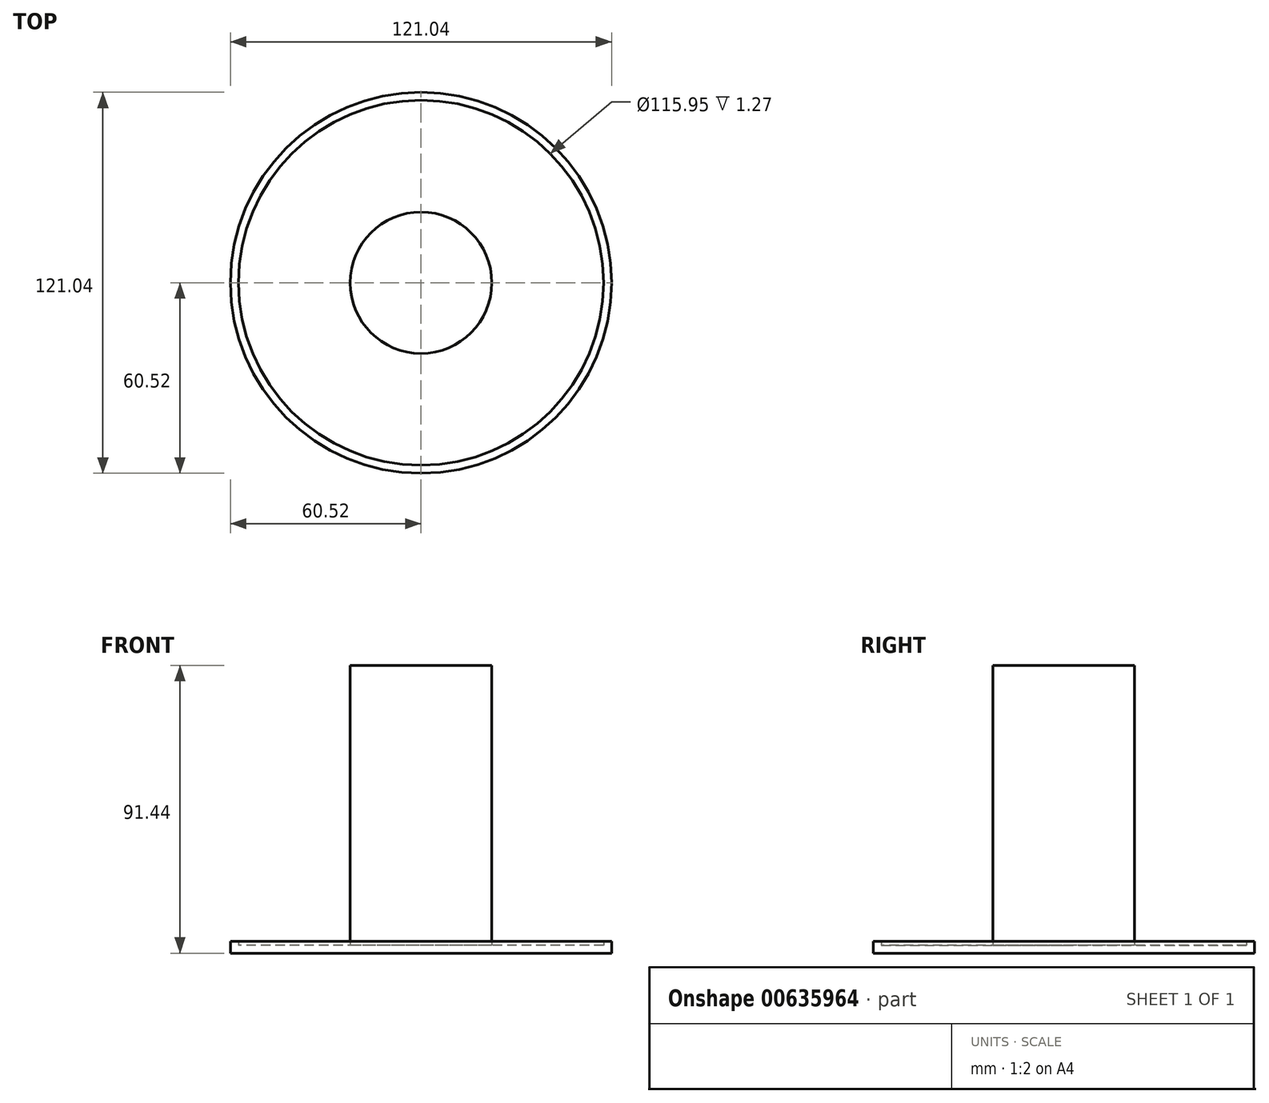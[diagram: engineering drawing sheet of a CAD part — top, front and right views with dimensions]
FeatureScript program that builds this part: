
annotation { "Feature Type Name" : "Feature", "Feature Type Description" : "" }
export const myFeature = defineFeature(function(context is Context, id is Id, definition is map)
    precondition{}
    {
        {
            var Q0;
            Q0=qCreatedBy(makeId("Top.planeOp"),FACE);
            var sketch = newSketch(context, id + "F0", { "sketchPlane" : qUnion([Q0])});
            skCircle(sketch, "E0", {"center": v(0, 0) * mm, "radius": 60.52 * mm});
            skSolve(sketch);
        }
        {
            var Q0;
            Q0 = qSketchRegion(id + "F0", true);
            extrude(context, id + "F1", {"entities" : qUnion([Q0]), "depth" : 3.8 * mm, "offsetDistance" : 25.4 * mm});
        }
        {
            var Q0;
            Q0=makeQuery(id+"F1.opExtrude","CAP_FACE",FACE,{"disambiguationData":[OSD([sQuery(id+"F0.wireOp",EDGE,"E0")])],"isStart":false});
            shell(context, id + "F2", {"entities" : qUnion([Q0]), "thickness" : 2.54 * mm});
        }
        {
            var Q0;
            {var subQ0=sQuery(id+"F0.wireOp",EDGE,"E0");Q0=makeQuery(id+"F2.opShell","OFFSET_FACE",FACE,{"disambiguationData":[OSD([subQ0]),TDD([makeQuery(id+"F1.opExtrude","CAP_FACE",FACE,{"disambiguationData":[OSD([subQ0])],"isStart":true})])]});}
            var sketch = newSketch(context, id + "F3", { "sketchPlane" : qUnion([Q0])});
            skCircle(sketch, "E1", {"center": v(0, 0) * mm, "radius": 22.48 * mm});
            skSolve(sketch);
        }
        {
            var Q0;
            Q0=makeQuery(id+"F3.imprint","IMPRINT",FACE,{"disambiguationData":[TD([[makeQuery(id+"F3.imprint","IMPRINT",EDGE,{"derivedFrom":sQuery(id+"F3.wireOp",EDGE,"E1")}),1.0]])]});
            extrude(context, id + "F4", {"entities" : qUnion([Q0]), "operationType" : NewBodyOperationType.ADD, "depth" : 88.9 * mm, "offsetDistance" : 25.4 * mm});
        }
    });
